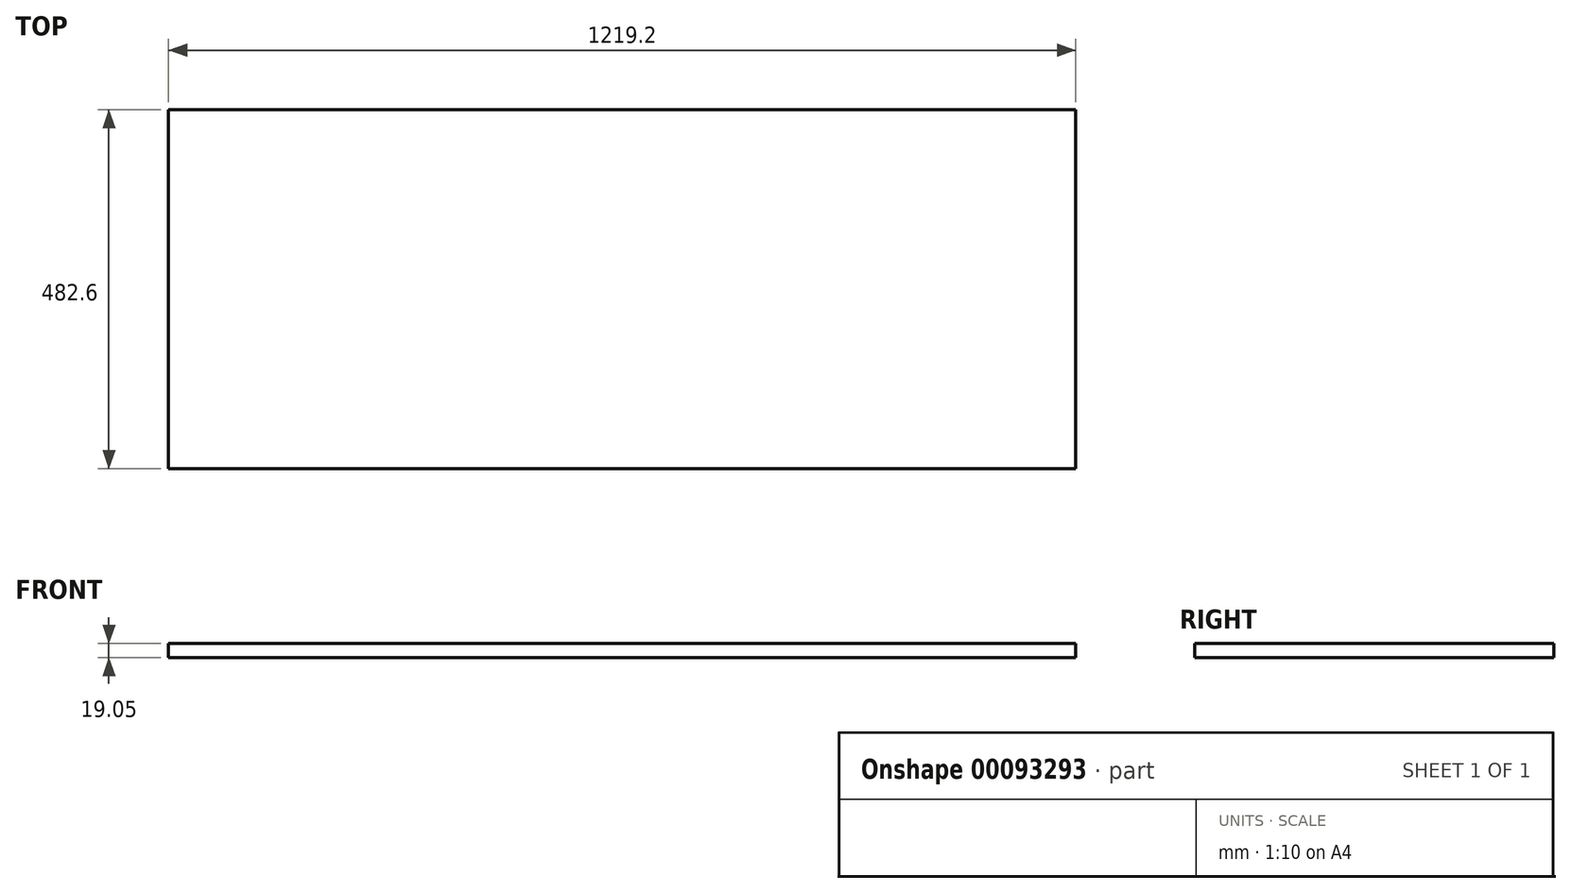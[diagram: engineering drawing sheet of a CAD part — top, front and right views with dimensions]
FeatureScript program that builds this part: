
annotation { "Feature Type Name" : "Feature", "Feature Type Description" : "" }
export const myFeature = defineFeature(function(context is Context, id is Id, definition is map)
    precondition{}
    {
        {
            var Q0;
            Q0=qCreatedBy(makeId("Top.planeOp"),FACE);
            var sketch = newSketch(context, id + "F0", { "sketchPlane" : qUnion([Q0])});
            skLineSegment(sketch, "E0.bottom", {"start": v(-641.17, -241.3) * mm, "end": v(578.03, -241.3) * mm});
            skLineSegment(sketch, "E0.top", {"start": v(-641.17, 241.3) * mm, "end": v(578.03, 241.3) * mm});
            skLineSegment(sketch, "E0.left", {"start": v(-641.17, -241.3) * mm, "end": v(-641.17, 241.3) * mm});
            skLineSegment(sketch, "E0.right", {"start": v(578.03, -241.3) * mm, "end": v(578.03, 241.3) * mm});
            skSolve(sketch);
        }
        {
            var Q0;
            Q0=makeQuery(id+"F0.imprint","IMPRINT",FACE,{"disambiguationData":[TD([[makeQuery(id+"F0.imprint","IMPRINT",EDGE,{"derivedFrom":sQuery(id+"F0.wireOp",EDGE,"E0.bottom")}),1.0]])]});
            extrude(context, id + "F1", {"entities" : qUnion([Q0]), "depth" : 19.05 * mm});
        }
    });
